# Revit family: Furniture_Shelving-Storage_KUMI_Vagghylla
name_source: partatom
category: Furniture
revit_build: Autodesk Revit 2018 (Build: 20190510_1515(x64)
units: mm (PartAtom-declared; Revit-internal decimal feet)

## family parameters
Cut with Voids When Loaded = No
Host = Face
OmniClass Number = 23.21.11.11.11
OmniClass Title = Commercial Storage Shelves
Room Calculation Point = No
Shared = No

## types (1)
- Furniture_Shelving-Storage_KUMI_Vagghylla
    BIMobject category = Shelving & Storage
    Default Elevation = 0 mm  [stored 0 ft]
    Description = Wall-mounted shelf system (additional section) that saves space and facilitates cleaning. It consists of 5 shelves in laminate (900x300 mm), 1 wall rail (1800 mm), 10 shelf brackets (300 mm) and 1 baseboard (1000 mm). All details are white. Maximum load can vary depending on wall construction and attachment.
    Design country = Sweden
    Edition number = 1
    Frame Material = Kumi - Steel - White
    Manufacturer = KUMI
    Manufacturer name = KUMI
    Material main = Steel
    Model = Wall shelf Storage including 5 Shelves Additional section White - 3-831-0
    Product Guid = 1c95c5cb-4a0b-40c3-85d0-3ad4e4c0dcea
    Product SKU = kumi-hyllsystem
    Product data url = https://bimobject.com
    Product name = Vägghylla
    Product url = https://www.kumi.se
    QR code = https://bimobject.com
    Shelves Material = Kumi - Laminate - White
    URL = https://www.kumi.se

note: [stored X ft] marks values corroborated as IEEE doubles in the binary element streams (Revit-internal decimal feet)

## geometry (parser evidence)
native form markers: Sweep x9
no freeform markers — native parametric forms only
